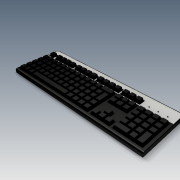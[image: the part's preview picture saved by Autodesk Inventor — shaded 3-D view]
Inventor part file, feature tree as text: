
AUTODESK INVENTOR PART (.ipt)
format: ipt  version: 2017 SP1 (Build 210196100, 196)  size: 758,784 bytes
history: native  units: mm
features: projected_geometry x10, extrude x5, sketch x5, fillet x2
ambient origin geometry x8: Origin, YZ Plane, XZ Plane, XY Plane, X Axis, Y Axis, Z Axis, Center Point
bodies: Solid1 (feature_tree)
feature tree (22):
  extrude  "Extrusion1"  Depth=160.0mm
  fillet  "Fillet1"  Radius=17.0mm
  extrude  "Extrusion2"  Depth=6.0mm
  sketch  "Sketch3"  dims[d9=4.0mm d10=102.0mm]
  extrude  "Extrusion5"  Depth=102.0mm
  extrude  "Extrusion6"  Depth=20.0mm
  extrude  "Extrusion7"  Depth=82.0mm
  fillet  "Fillet2"  Radius=5.0mm
  sketch  "Sketch1"  dims[d0=450.0mm d2=160.0mm d3=17.0mm d4=0.0mm]
  sketch  "Sketch2"  dims[d5=10.0mm d6=5.0mm d7=6.0mm]
  projected_geometry  "Projected Loop1"
  projected_geometry  "Projected Loop2"
  projected_geometry  "Projected Loop3"
  projected_geometry  "Projected Loop4"
  projected_geometry  "Projected Loop5"
  projected_geometry  "Projected Loop6"
  projected_geometry  "Projected Loop7"
  projected_geometry  "Projected Loop8"
  projected_geometry  "Projected Loop10"
  sketch  "Sketch5"  dims[d12=22.0mm d13=20.0mm]
  sketch  "Sketch6"  dims[d15=22.0mm d17=82.0mm d18=5.0mm d19=22.0mm d20=6.0mm d21=22.0mm d22=82.0mm d24=82.0mm d26=82.0mm d27=42.0mm d28=4.0mm d29=50.0mm d30=15.0mm d31=5.0mm d32=0.0mm d33=2.0mm d34=2.0mm d35=2.0mm d36=2.0mm d37=2.0mm d38=18.0mm d39=2.0mm d40=2.0mm d41=2.0mm d42=2.0mm d43=18.0mm d44=18.0mm d45=2.0mm d47=18.0mm d51=2.0mm d52=2.0mm d53=2.0mm d87=4.0mm d88=4.0mm d89=282.0mm d90=5.0mm d91=20.0mm d92=62.0mm d93=2.0mm d94=2.0mm d95=18.0mm d96=30.0mm d98=20.0mm d99=20.0mm d101=20.0mm d104=18.0mm d105=2.0mm d106=18.0mm d107=2.0mm d108=18.0mm d109=18.0mm d132=2.0mm d133=2.0mm d134=1.0mm d135=0.0mm d136=2.0mm d137=2.0mm d139=13.0mm d140=-1.745329mm d141=2.0mm d142=2.0mm d143=18.0mm d144=18.0mm d151=2.0mm d152=2.0mm d153=18.0mm d154=18.0mm d161=13.0mm d162=-1.745329mm d163=62.0mm d164=4.0mm d165=2.0mm]
  projected_geometry  "Projected Loop11"
